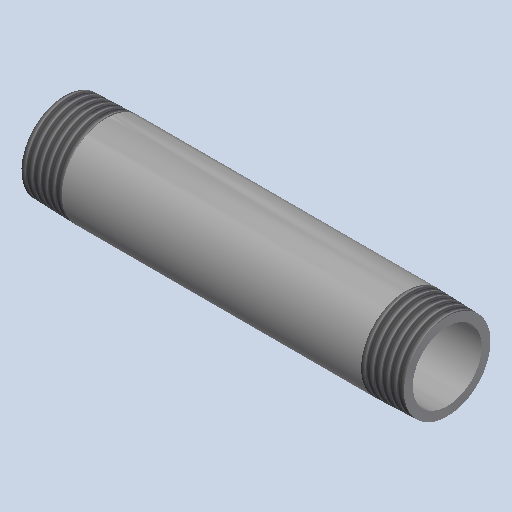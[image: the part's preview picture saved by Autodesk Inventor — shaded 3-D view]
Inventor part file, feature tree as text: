
AUTODESK INVENTOR PART (.ipt)
format: ipt  version: 2025 (Build 290162000, 162)  size: 201,728 bytes
history: native  units: mm (DEFAULTED — no unit token found)
features: other x8, revolve x1
ambient origin geometry x8: Origin, YZ Plane, XZ Plane, XY Plane, X Axis, Y Axis, Z Axis, Center Point
bodies: Solid1 (feature_tree)
feature tree (9):
  revolve  "Revolution1"  [1 undecoded]
  other  "Work Axis1"
  other  "Work Point5"
  other  "Work Axis2"
  other  "Work Point6"
  other  "Work Axis3"
  other  "Work Axis4"
  other  "Work Point7"
  other  "Work Point8"
note: 1 required parameter value undecoded (feature->parameter linkage not recoverable at this tier; creation-order binding heuristic only, values carry confidence <= 0.55)
